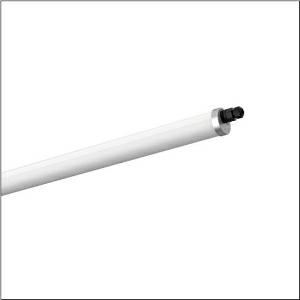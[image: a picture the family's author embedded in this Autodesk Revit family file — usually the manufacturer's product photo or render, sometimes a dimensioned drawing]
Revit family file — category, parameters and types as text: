
# Revit family: monsun_r__31_tube_51ft10dn480a_9fe9
name_source: partatom
category: Lighting Fixtures
units: mm (PartAtom-declared; Revit-internal decimal feet)

## family parameters
Cut with Voids When Loaded = No
Host = Face
Light Source = No
Part Type = Normal
Room Calculation Point = No
Round Connector Dimension = Use Diameter
Shared = No

## types (1)
- Monsun® 31 Tube (1 x LED, 8000 lm, 50 W, 4000K)
    Apparent Load = 50 VA
    CIE Flux Codes = 42 71 89 91 100
    Color Rendering = 80
    Color Temperature = 4000K
    Default Elevation = 1800 mm
    Description = Monsun® 31 Tube, tubular luminaire, primary optical cover: diffuser, of PMMA, light emission: direct distribution, primary light characteristic: symmetric, installation type: suspended mounting, surface-mounted, LED, rated luminous flux: 8.000lm, luminous efficacy: 160lm/W, light colour: 840, colour temperature: 4000K, control gear: DALI 2, with with 1 terminal, 5-pole, max. 2.5mm², through-wiring: 5x 1.5mm², mains connection: 220..240V, AC, 50/60Hz, rated input power: 50W, housing, cylindrical, of PMMA, semi-transparent, matt white, with luminaire and ceiling fastening, V4A, mounting with brackets of stainless steel, length: 1.570mm, diameter: 75mm, end cap, of stainless steel (V4A), protection rating (complete): IP67/IP69K, insulation class (complete): insulation class I (protective earthing), certification: CE, UKCA, impact resistance: IK07, permissible operating ambient temperature: -20..+40°C, corresponds to IFS (International Featured Standards) requirements for safety and quality in the food industry, usage in unprotected outdoor areas possible with horizontal mounting, contact your sales advisor before using the luminaires in applications with unclear chemical exposure, large temperature fluctuations or condensation-forming humidity, packaging unit: 1 piece
    Height = 83 mm
    Lamp = 1 x LED
    Lamp Light Flux = 8000 lm
    Lamp Power = 50 W
    Lamp count = 1
    Length = 1570 mm
    Luminous efficacy = 160 lm/W
    Manufacturer = Siteco
    ModVariant = No
    Model = 51FT10DN480A
    Mounting Place = Ceiling
    Mounting Type = Pendant
    Number of Poles = 1
    OnlyDefault = Yes
    Power Factor = 1
    Product Name = Monsun® 31 Tube
    Product group = tubular luminaire
    ProductGroupID = 907
    Protection Class = Protection class I
    RLX_Detail_Level = 1
    RLX_Emergency_Light_Flux = 0 lm
    RLX_Emergency_Type = 0
    RLX_Emergency_Type_DB = No
    RlxData = <blob elided: 25453 chars, md5=8d6da987>
    Socket = socket
    Standby Power = 0 W
    System Light Flux = 8000 lm
    System Power = 50 W
    Type Comments = Product without accessories
    Type Image = l_1228461.jpg
    URL = http://relux.com
    VarID = ---
    Voltage = 0 V
    Weight = 0.00 kg
    Width = 75 mm

## geometry (parser evidence)
native form markers: Blend x4, Sweep x13
no freeform markers — native parametric forms only
